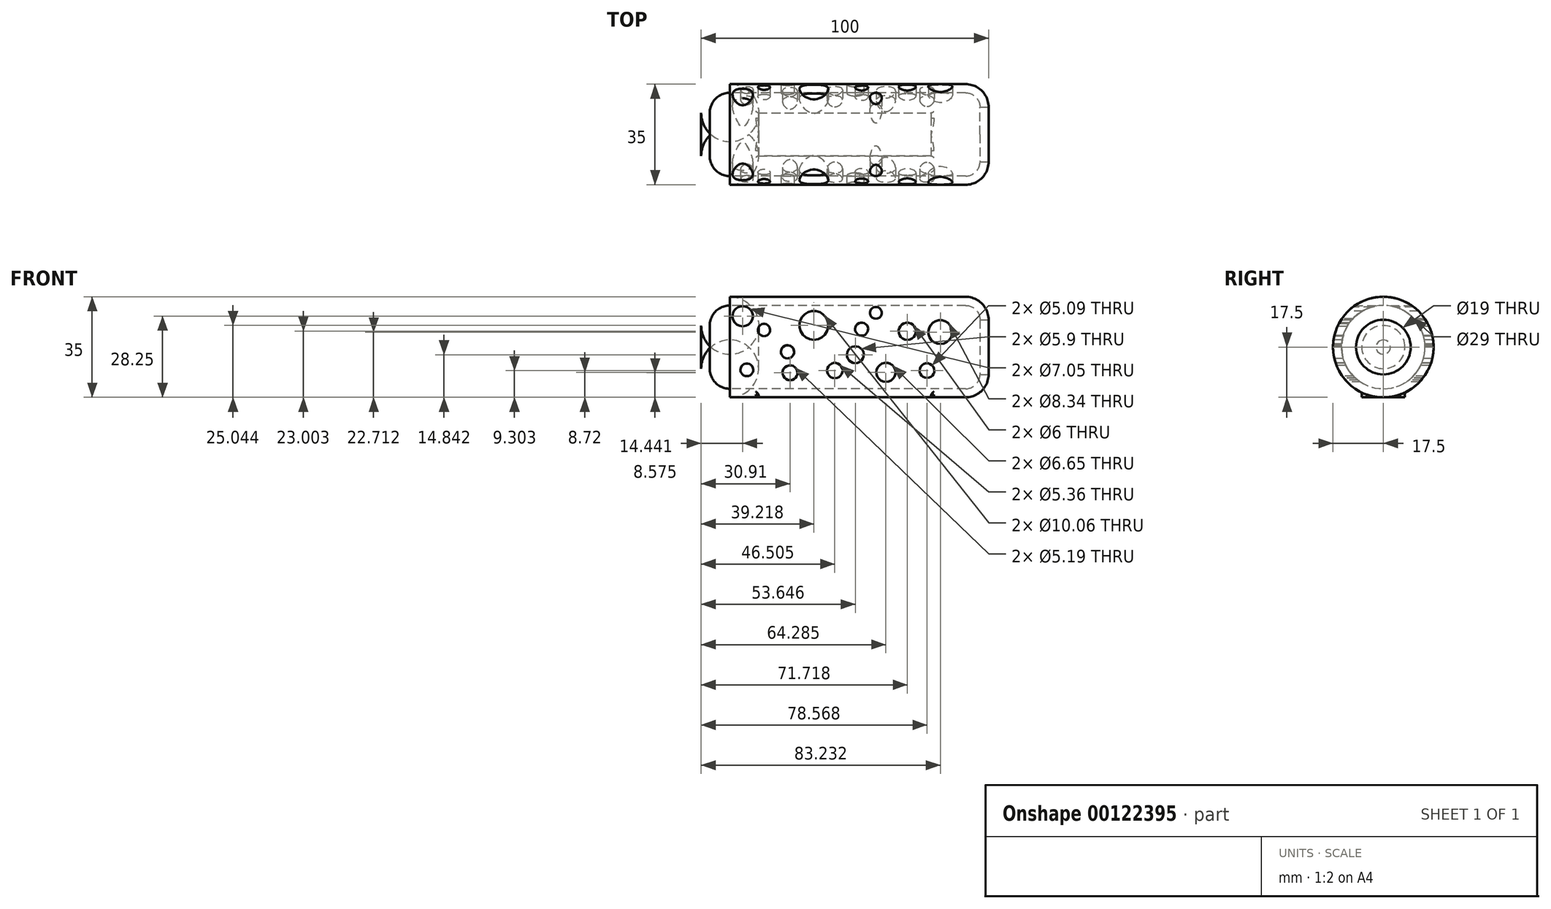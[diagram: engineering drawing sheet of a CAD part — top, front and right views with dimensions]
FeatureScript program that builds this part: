
annotation { "Feature Type Name" : "Feature", "Feature Type Description" : "" }
export const myFeature = defineFeature(function(context is Context, id is Id, definition is map)
    precondition{}
    {
        {
            var Q0;
            Q0=qCreatedBy(makeId("Right.planeOp"),FACE);
            var sketch = newSketch(context, id + "F0", { "sketchPlane" : qUnion([Q0])});
            skCircle(sketch, "E0", {"center": v(0, 0) * mm, "radius": 17.5 * mm});
            skSolve(sketch);
        }
        {
            var Q0;
            Q0=makeQuery(id+"F0.imprint","IMPRINT",FACE,{"disambiguationData":[TD([[makeQuery(id+"F0.imprint","IMPRINT",EDGE,{"derivedFrom":sQuery(id+"F0.wireOp",EDGE,"E0")}),1.0]])]});
            extrude(context, id + "F1", {"entities" : qUnion([Q0]), "depth" : 100 * mm});
        }
        {
            var Q0;
            Q0=makeQuery(id+"F1.opExtrude","CAP_EDGE",EDGE,{"disambiguationData":[OSD([sQuery(id+"F0.wireOp",EDGE,"E0")])],"isStart":true});
            fillet(context, id + "F2", {"entities" : qUnion([Q0]), "radius" : 10 * mm, "tangentPropagation" : true, "allowEdgeOverflow" : false});
        }
        {
            var Q0;
            Q0=makeQuery(id+"F1.opExtrude","CAP_EDGE",EDGE,{"disambiguationData":[OSD([sQuery(id+"F0.wireOp",EDGE,"E0")])],"isStart":false});
            fillet(context, id + "F3", {"entities" : qUnion([Q0]), "radius" : 8 * mm, "tangentPropagation" : true, "allowEdgeOverflow" : false});
        }
        {
            var Q0;
            Q0=makeQuery(id+"F1.opExtrude","CAP_FACE",FACE,{"disambiguationData":[OSD([sQuery(id+"F0.wireOp",EDGE,"E0")])],"isStart":false});
            shell(context, id + "F4", {"entities" : qUnion([Q0]), "thickness" : 3 * mm});
        }
        {
            var Q0;
            Q0=qCreatedBy(makeId("Top.planeOp"),FACE);
            cPlane(context, id + "F5", {"entities" : qUnion([Q0]), "cplaneType" : CPlaneType.OFFSET, "offset" : 15 * mm, "oppositeDirection" : true, "width" : 150 * mm, "height" : 150 * mm});
        }
        {
            var Q0;
            Q0=qCreatedBy(id+"F5.planeOp",FACE);
            var sketch = newSketch(context, id + "F6", { "sketchPlane" : qUnion([Q0])});
            skLineSegment(sketch, "E1.bottom", {"start": v(20, 7.5) * mm, "end": v(80, 7.5) * mm});
            skLineSegment(sketch, "E1.top", {"start": v(20, -7.5) * mm, "end": v(80, -7.5) * mm});
            skLineSegment(sketch, "E1.left", {"start": v(20, 7.5) * mm, "end": v(20, -7.5) * mm});
            skLineSegment(sketch, "E1.right", {"start": v(80, 7.5) * mm, "end": v(80, -7.5) * mm});
            skSolve(sketch);
        }
        {
            var Q0;
            Q0 = qSketchRegion(id + "F6", true);
            extrude(context, id + "F7", {"entities" : qUnion([Q0]), "operationType" : NewBodyOperationType.ADD, "oppositeDirection" : true, "depth" : 2.5 * mm});
        }
        {
            var Q0;
            Q0=makeQuery(id+"F7.boolean.opBoolean","INTERSECT",EDGE,{"derivedFrom":[makeQuery(id+"F1.opExtrude","SWEPT_FACE",FACE,{"disambiguationData":[OSD([sQuery(id+"F0.wireOp",EDGE,"E0")])]}),makeQuery(id+"F7.opExtrude","SWEPT_FACE",FACE,{"disambiguationData":[OSD([sQuery(id+"F6.wireOp",EDGE,"E1.bottom")])]})]});
            var Q1;
            Q1=makeQuery(id+"F7.boolean.opBoolean","INTERSECT",EDGE,{"derivedFrom":[makeQuery(id+"F1.opExtrude","SWEPT_FACE",FACE,{"disambiguationData":[OSD([sQuery(id+"F0.wireOp",EDGE,"E0")])]}),makeQuery(id+"F7.opExtrude","SWEPT_FACE",FACE,{"disambiguationData":[OSD([sQuery(id+"F6.wireOp",EDGE,"E1.top")])]})]});
            var Q2;
            Q2=makeQuery(id+"F7.boolean.opBoolean","INTERSECT",EDGE,{"disambiguationData":[OD(1.0)],"derivedFrom":[makeQuery(id+"F1.opExtrude","SWEPT_FACE",FACE,{"disambiguationData":[OSD([sQuery(id+"F0.wireOp",EDGE,"E0")])]}),makeQuery(id+"F7.opExtrude","SWEPT_FACE",FACE,{"disambiguationData":[OSD([sQuery(id+"F6.wireOp",EDGE,"E1.right")])]})]});
            var Q3;
            Q3=makeQuery(id+"F7.boolean.opBoolean","INTERSECT",EDGE,{"disambiguationData":[OD(1.0)],"derivedFrom":[makeQuery(id+"F1.opExtrude","SWEPT_FACE",FACE,{"disambiguationData":[OSD([sQuery(id+"F0.wireOp",EDGE,"E0")])]}),makeQuery(id+"F7.opExtrude","SWEPT_FACE",FACE,{"disambiguationData":[OSD([sQuery(id+"F6.wireOp",EDGE,"E1.left")])]})]});
            fillet(context, id + "F8", {"entities" : qUnion([Q0, Q1, Q2, Q3]), "radius" : 1 * mm, "tangentPropagation" : true, "allowEdgeOverflow" : false});
        }
        {
            var Q0;
            Q0=qCreatedBy(makeId("Front.planeOp"),FACE);
            var sketch = newSketch(context, id + "F9", { "sketchPlane" : qUnion([Q0])});
            skCircle(sketch, "E2", {"center": v(15.9, -7.9) * mm, "radius": 2.22 * mm});
            skCircle(sketch, "E3", {"center": v(21.87, 5.94) * mm, "radius": 2.15 * mm});
            skCircle(sketch, "E4", {"center": v(30.91, -8.93) * mm, "radius": 2.6 * mm});
            skCircle(sketch, "E5", {"center": v(39.22, 7.54) * mm, "radius": 5.03 * mm});
            skCircle(sketch, "E6", {"center": v(46.5, -8.2) * mm, "radius": 2.68 * mm});
            skCircle(sketch, "E7", {"center": v(55.83, 6.23) * mm, "radius": 2.27 * mm});
            skCircle(sketch, "E8", {"center": v(64.29, -8.78) * mm, "radius": 3.32 * mm});
            skCircle(sketch, "E9", {"center": v(71.72, 5.5) * mm, "radius": 3 * mm});
            skCircle(sketch, "E10", {"center": v(83.23, 5.21) * mm, "radius": 4.17 * mm});
            skCircle(sketch, "E11", {"center": v(78.57, -8.2) * mm, "radius": 2.55 * mm});
            skCircle(sketch, "E12", {"center": v(53.65, -2.66) * mm, "radius": 2.95 * mm});
            skCircle(sketch, "E13", {"center": v(30.04, -1.64) * mm, "radius": 2.3 * mm});
            skCircle(sketch, "E14", {"center": v(14.44, 10.75) * mm, "radius": 3.53 * mm});
            skCircle(sketch, "E15", {"center": v(60.79, 11.92) * mm, "radius": 2.06 * mm});
            skSolve(sketch);
        }
        {
            var Q0;
            Q0 = qSketchRegion(id + "F9", true);
            var Q1;
            Q1=makeQuery(id+"F1.opExtrude","SWEPT_FACE",FACE,{"disambiguationData":[OSD([sQuery(id+"F0.wireOp",EDGE,"E0")])]});
            extrude(context, id + "F10", {"entities" : qUnion([Q0]), "operationType" : NewBodyOperationType.REMOVE, "oppositeDirection" : true, "depth" : 21.6 * mm, "hasSecondDirection" : true, "secondDirectionOppositeDirection" : false, "secondDirectionBoundEntityFace" : qUnion([Q1]), "secondDirectionDepth" : 25 * mm});
        }
    });
